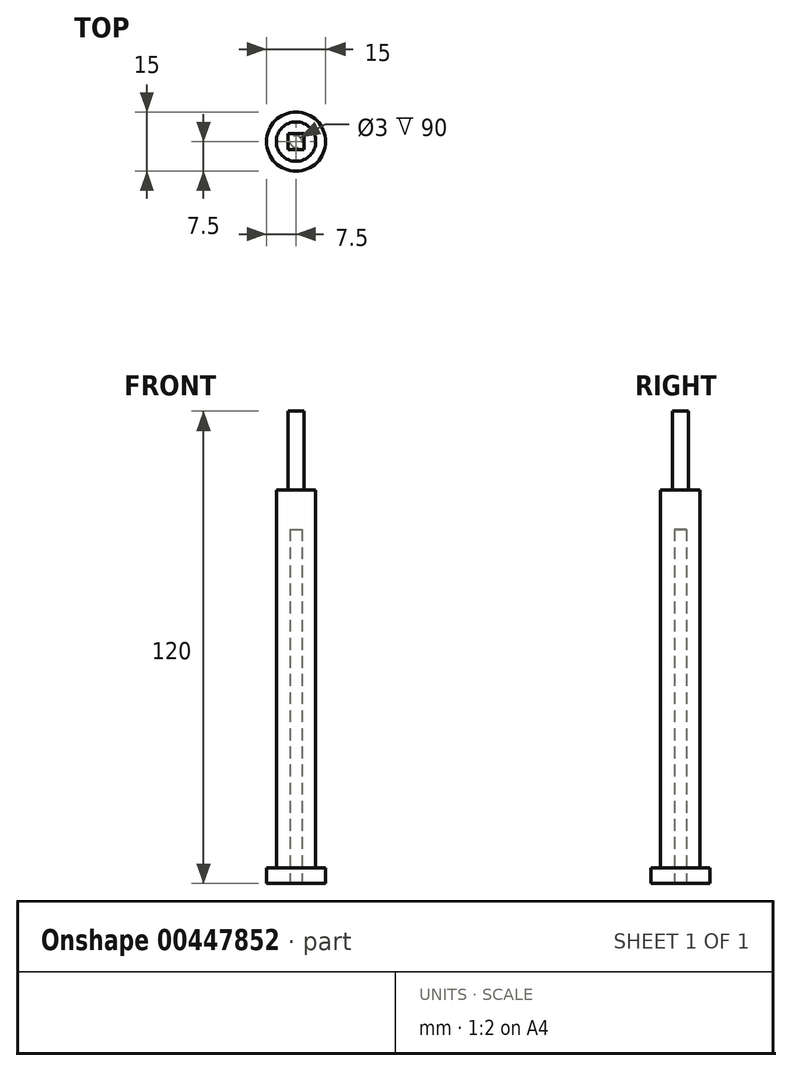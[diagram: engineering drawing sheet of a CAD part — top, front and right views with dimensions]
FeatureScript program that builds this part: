
annotation { "Feature Type Name" : "Feature", "Feature Type Description" : "" }
export const myFeature = defineFeature(function(context is Context, id is Id, definition is map)
    precondition{}
    {
        {
            var Q0;
            Q0=qCreatedBy(makeId("Top.planeOp"),FACE);
            var sketch = newSketch(context, id + "F0", { "sketchPlane" : qUnion([Q0])});
            skCircle(sketch, "E0", {"center": v(0, 0) * mm, "radius": 7.5 * mm});
            skSolve(sketch);
        }
        {
            var Q0;
            Q0=qSketchRegion(id+"F0",true);
            extrude(context, id + "F1", {"entities" : qUnion([Q0]), "depth" : 4 * mm});
        }
        {
            var Q0;
            Q0=qCreatedBy(makeId("Top.planeOp"),FACE);
            var sketch = newSketch(context, id + "F2", { "sketchPlane" : qUnion([Q0])});
            skCircle(sketch, "E1", {"center": v(0, 0) * mm, "radius": 5 * mm});
            skSolve(sketch);
        }
        {
            var Q0;
            Q0=qSketchRegion(id+"F2",true);
            extrude(context, id + "F3", {"entities" : qUnion([Q0]), "operationType" : NewBodyOperationType.ADD, "depth" : 100 * mm});
        }
        {
            var Q0;
            Q0=makeQuery(id+"F3.opExtrude","CAP_FACE",FACE,{"disambiguationData":[OSD([sQuery(id+"F2.wireOp",EDGE,"E1")])],"isStart":false});
            var sketch = newSketch(context, id + "F4", { "sketchPlane" : qUnion([Q0])});
            skLineSegment(sketch, "E2.bottom", {"start": v(-2, 2) * mm, "end": v(2, 2) * mm});
            skLineSegment(sketch, "E2.top", {"start": v(-2, -2) * mm, "end": v(2, -2) * mm});
            skLineSegment(sketch, "E2.left", {"start": v(-2, 2) * mm, "end": v(-2, -2) * mm});
            skLineSegment(sketch, "E2.right", {"start": v(2, 2) * mm, "end": v(2, -2) * mm});
            skSolve(sketch);
        }
        {
            var Q0;
            Q0=makeQuery(id+"F4.imprint","IMPRINT",FACE,{"disambiguationData":[TD([[makeQuery(id+"F4.imprint","IMPRINT",EDGE,{"derivedFrom":sQuery(id+"F4.wireOp",EDGE,"E2.bottom")}),-1.0]])]});
            extrude(context, id + "F5", {"entities" : qUnion([Q0]), "operationType" : NewBodyOperationType.ADD, "depth" : 20 * mm});
        }
        {
            var Q0;
            Q0=makeQuery(id+"F1.opExtrude","CAP_FACE",FACE,{"disambiguationData":[OSD([sQuery(id+"F0.wireOp",EDGE,"E0")])],"isStart":true});
            var sketch = newSketch(context, id + "F6", { "sketchPlane" : qUnion([Q0])});
            skCircle(sketch, "E3", {"center": v(0, 0) * mm, "radius": 1.5 * mm});
            skSolve(sketch);
        }
        {
            var Q0;
            Q0=qSketchRegion(id+"F6",true);
            extrude(context, id + "F7", {"entities" : qUnion([Q0]), "operationType" : NewBodyOperationType.REMOVE, "oppositeDirection" : true, "depth" : 90 * mm});
        }
    });
